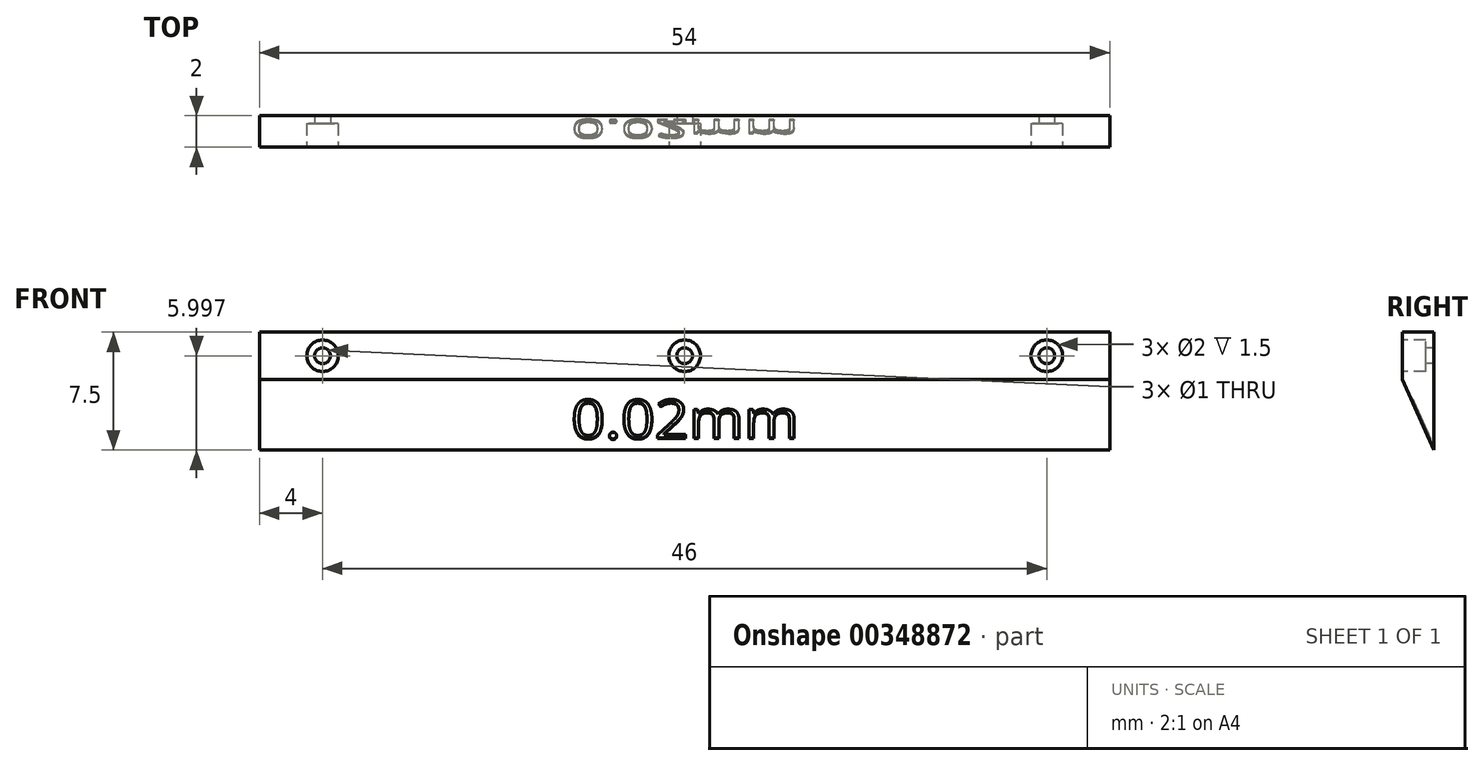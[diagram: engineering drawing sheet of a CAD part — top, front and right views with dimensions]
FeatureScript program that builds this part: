
annotation { "Feature Type Name" : "Feature", "Feature Type Description" : "" }
export const myFeature = defineFeature(function(context is Context, id is Id, definition is map)
    precondition{}
    {
        {
            var Q0;
            Q0=qCreatedBy(makeId("Front.planeOp"),FACE);
            var sketch = newSketch(context, id + "F0", { "sketchPlane" : qUnion([Q0])});
            skLineSegment(sketch, "E0.bottom", {"start": v(0, 0) * mm, "end": v(54, 0) * mm});
            skLineSegment(sketch, "E0.top", {"start": v(0, 7.5) * mm, "end": v(54, 7.5) * mm});
            skLineSegment(sketch, "E0.left", {"start": v(0, 0) * mm, "end": v(0, 7.5) * mm});
            skLineSegment(sketch, "E0.right", {"start": v(54, 0) * mm, "end": v(54, 7.5) * mm});
            skSolve(sketch);
        }
        {
            var Q0;
            Q0=qSketchRegion(id+"F0",true);
            extrude(context, id + "F1", {"entities" : qUnion([Q0]), "depth" : 2 * mm});
        }
        {
            var Q0;
            Q0=makeQuery(id+"F1.opExtrude","SWEPT_FACE",FACE,{"disambiguationData":[OSD([sQuery(id+"F0.wireOp",EDGE,"E0.right")])]});
            var sketch = newSketch(context, id + "F2", { "sketchPlane" : qUnion([Q0])});
            skLineSegment(sketch, "E1", {"start": v(0, 0) * mm, "end": v(-2, 4.5) * mm});
            skLineSegment(sketch, "E2", {"start": v(-2, 4.5) * mm, "end": v(-2, 0) * mm});
            skLineSegment(sketch, "E3", {"start": v(-2, 0) * mm, "end": v(0, 0) * mm});
            skSolve(sketch);
        }
        {
            var Q0;
            Q0=qSketchRegion(id+"F2",true);
            extrude(context, id + "F3", {"entities" : qUnion([Q0]), "operationType" : NewBodyOperationType.REMOVE, "endBound" : BoundingType.THROUGH_ALL, "oppositeDirection" : true, "depth" : 25 * mm});
        }
        {
            var Q0;
            Q0=makeQuery(id+"F1.opExtrude","CAP_FACE",FACE,{"disambiguationData":[OSD([sQuery(id+"F0.wireOp",EDGE,"E0.bottom"),sQuery(id+"F0.wireOp",EDGE,"E0.top"),sQuery(id+"F0.wireOp",EDGE,"E0.left"),sQuery(id+"F0.wireOp",EDGE,"E0.right")])],"isStart":false});
            var sketch = newSketch(context, id + "F4", { "sketchPlane" : qUnion([Q0])});
            skCircle(sketch, "E4", {"center": v(4, 6) * mm, "radius": 1 * mm});
            skCircle(sketch, "E5", {"center": v(27, 6) * mm, "radius": 1 * mm});
            skCircle(sketch, "E6", {"center": v(50, 6) * mm, "radius": 1 * mm});
            skSolve(sketch);
        }
        {
            var Q0;
            Q0=qSketchRegion(id+"F4",true);
            extrude(context, id + "F5", {"entities" : qUnion([Q0]), "operationType" : NewBodyOperationType.REMOVE, "oppositeDirection" : true, "depth" : 1.5 * mm});
        }
        {
            var Q0;
            Q0=makeQuery(id+"F5.boolean.opBoolean","COPY",FACE,{"derivedFrom":makeQuery(id+"F5.opExtrude","CAP_FACE",FACE,{"disambiguationData":[OSD([sQuery(id+"F4.wireOp",EDGE,"E4")])],"isStart":false})});
            var sketch = newSketch(context, id + "F6", { "sketchPlane" : qUnion([Q0])});
            skCircle(sketch, "E7", {"center": v(4, 6) * mm, "radius": 0.5 * mm});
            skCircle(sketch, "E8", {"center": v(27, 6) * mm, "radius": 0.5 * mm});
            skCircle(sketch, "E9", {"center": v(50, 6) * mm, "radius": 0.5 * mm});
            skSolve(sketch);
        }
        {
            var Q0;
            Q0=qSketchRegion(id+"F6",true);
            extrude(context, id + "F7", {"entities" : qUnion([Q0]), "operationType" : NewBodyOperationType.REMOVE, "endBound" : BoundingType.THROUGH_ALL, "oppositeDirection" : true, "depth" : 25 * mm});
        }
        {
            var Q0;
            Q0=makeQuery(id+"F3.boolean.opBoolean","COPY",FACE,{"derivedFrom":makeQuery(id+"F3.opExtrude","SWEPT_FACE",FACE,{"disambiguationData":[OSD([sQuery(id+"F2.wireOp",EDGE,"E1")])]})});
            var sketch = newSketch(context, id + "F8", { "sketchPlane" : qUnion([Q0])});
            skText(sketch, "E10", { "text": "0.02mm", "fontName": "OpenSans-Regular.ttf"});
            skLineSegment(sketch, "E11", {"start": v(0, 0.8) * mm, "end": v(54, 0.8) * mm, "construction": true});
            const initialGuessF8  = {"E10": [0.0198, 0.0008, 1, 0, 0.00271]};
            skSetInitialGuess(sketch, initialGuessF8);
            skSolve(sketch);
        }
        {
            var Q0;
            Q0=qSketchRegion(id+"F8",true);
            extrude(context, id + "F9", {"entities" : qUnion([Q0]), "operationType" : NewBodyOperationType.REMOVE, "oppositeDirection" : true, "depth" : 0.1 * mm});
        }
    });
